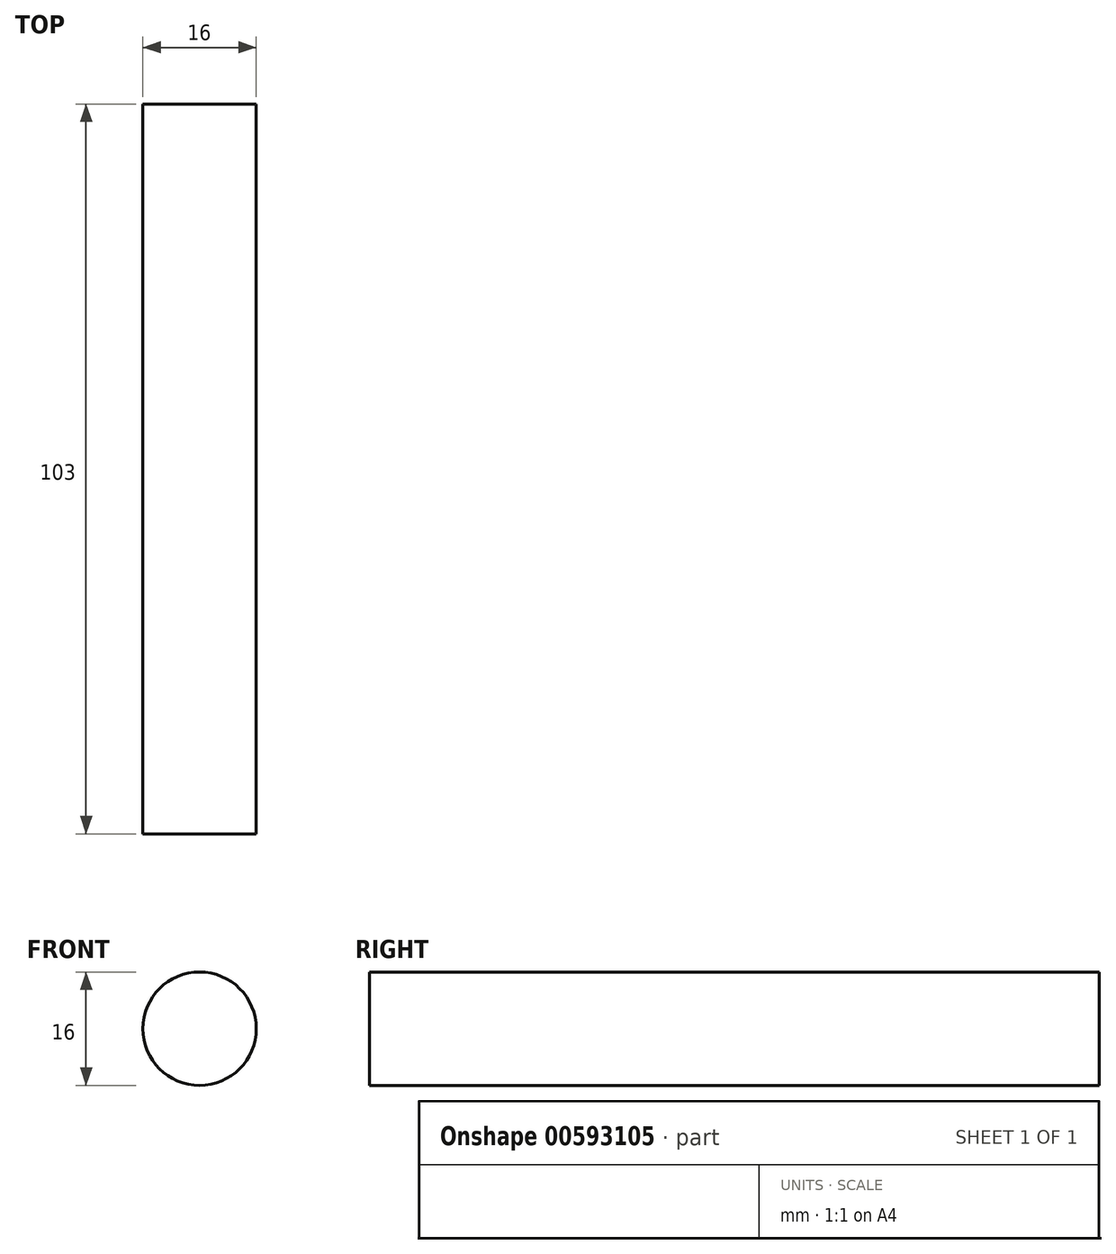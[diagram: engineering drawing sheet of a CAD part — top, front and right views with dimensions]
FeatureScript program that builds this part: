
annotation { "Feature Type Name" : "Feature", "Feature Type Description" : "" }
export const myFeature = defineFeature(function(context is Context, id is Id, definition is map)
    precondition{}
    {
        {
            var Q0;
            Q0=qCreatedBy(makeId("Front.planeOp"),FACE);
            var sketch = newSketch(context, id + "F0", { "sketchPlane" : qUnion([Q0])});
            skCircle(sketch, "E0", {"center": v(0, 0) * mm, "radius": 8 * mm});
            skSolve(sketch);
        }
        {
            var Q0;
            Q0=qSketchRegion(id+"F0",true);
            extrude(context, id + "F1", {"entities" : qUnion([Q0]), "depth" : 103 * mm, "offsetDistance" : 25 * mm});
        }
    });
